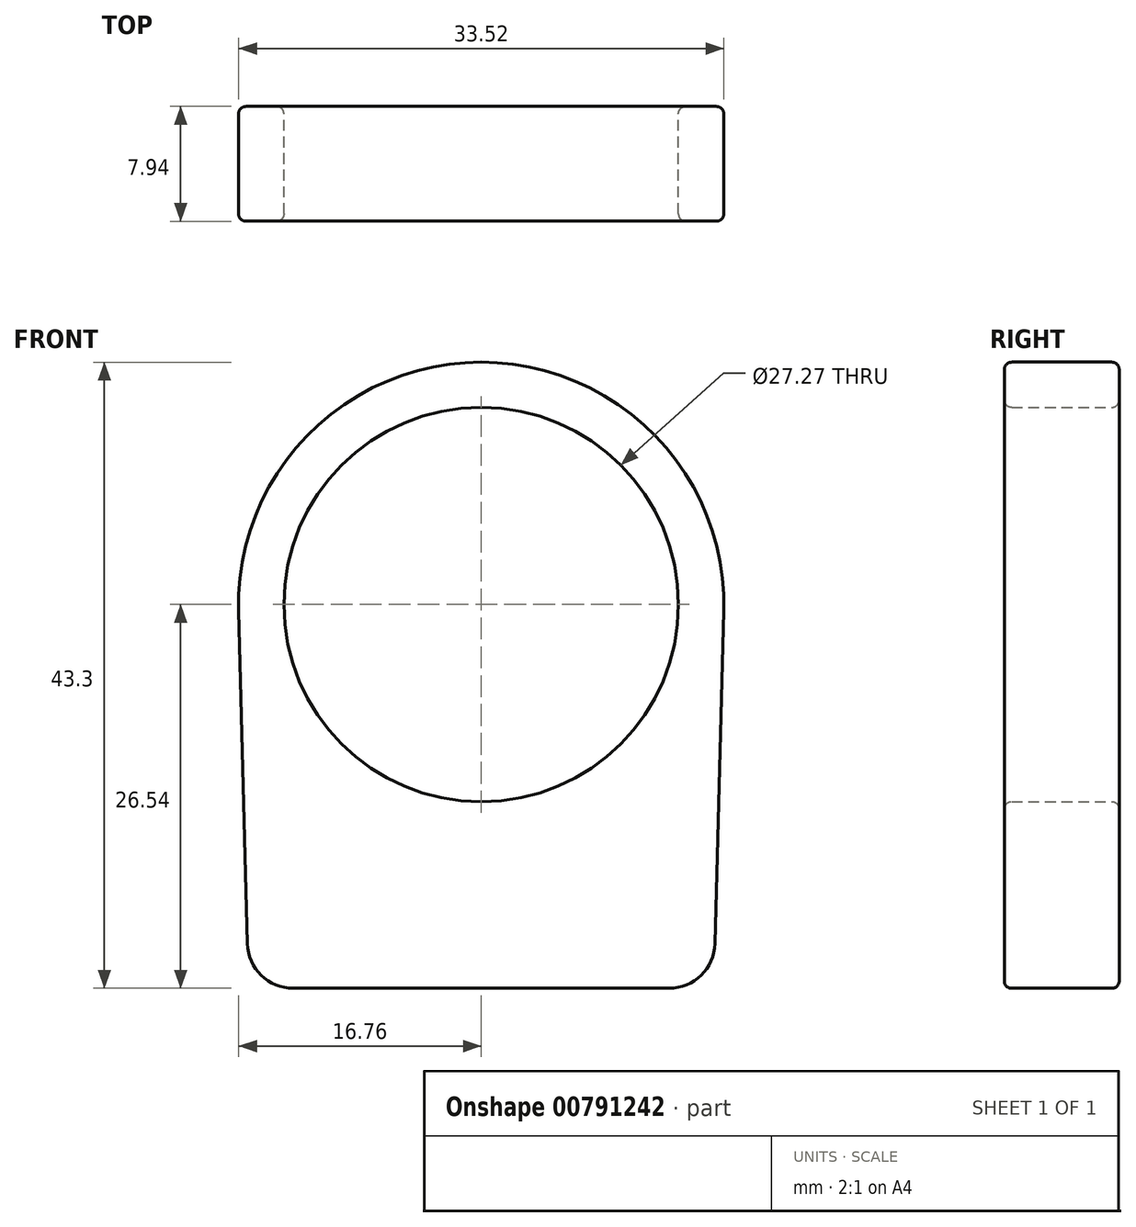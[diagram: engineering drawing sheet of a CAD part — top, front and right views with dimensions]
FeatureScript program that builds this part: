
annotation { "Feature Type Name" : "Feature", "Feature Type Description" : "" }
export const myFeature = defineFeature(function(context is Context, id is Id, definition is map)
    precondition{}
    {
        {
            var Q0;
            Q0=qCreatedBy(makeId("Front.planeOp"),FACE);
            var sketch = newSketch(context, id + "F0", { "sketchPlane" : qUnion([Q0])});
            skCircle(sketch, "E0", {"center": v(0, 0) * mm, "radius": 13.63 * mm});
            skArc(sketch, "E1", {"start": v(16.76, -0.44) * mm, "mid": v(0, 16.76) * mm, "end": v(-16.76, -0.44) * mm});
            skLineSegment(sketch, "E2", {"start": v(-12.98, -26.54) * mm, "end": v(12.98, -26.54) * mm});
            skLineSegment(sketch, "E3", {"start": v(-16.16, -23.45) * mm, "end": v(-16.76, -0.44) * mm});
            skLineSegment(sketch, "E4", {"start": v(16.16, -23.45) * mm, "end": v(16.76, -0.44) * mm});
            skPoint(sketch, "E5", {"position": v(0, -26.54) * mm});
            skPoint(sketch, "E6.visualSharp", {"position": v(-16.07, -26.54) * mm});
            skArc(sketch, "E6.filletArc", {"start": v(-16.16, -23.45) * mm, "mid": v(-15.2, -25.64) * mm, "end": v(-12.98, -26.54) * mm});
            skPoint(sketch, "E7.visualSharp", {"position": v(16.07, -26.54) * mm});
            skArc(sketch, "E7.filletArc", {"start": v(12.98, -26.54) * mm, "mid": v(15.2, -25.64) * mm, "end": v(16.16, -23.45) * mm});
            skSolve(sketch);
        }
        {
            var Q0;
            Q0=qSketchRegion(id+"F0",true);
            extrude(context, id + "F1", {"entities" : qUnion([Q0]), "endBound" : BoundingType.SYMMETRIC, "depth" : 7.94 * mm});
        }
        {
            var Q0;
            Q0=makeQuery(id+"F1.opExtrude","CAP_FACE",FACE,{"disambiguationData":[OSD([sQuery(id+"F0.wireOp",EDGE,"E0"),sQuery(id+"F0.wireOp",EDGE,"E1"),sQuery(id+"F0.wireOp",EDGE,"E2"),sQuery(id+"F0.wireOp",EDGE,"E3"),sQuery(id+"F0.wireOp",EDGE,"E4"),sQuery(id+"F0.wireOp",EDGE,"E6.filletArc"),sQuery(id+"F0.wireOp",EDGE,"E7.filletArc")])],"isStart":false});
            var Q1;
            Q1=makeQuery(id+"F1.opExtrude","CAP_FACE",FACE,{"disambiguationData":[OSD([sQuery(id+"F0.wireOp",EDGE,"E0"),sQuery(id+"F0.wireOp",EDGE,"E1"),sQuery(id+"F0.wireOp",EDGE,"E2"),sQuery(id+"F0.wireOp",EDGE,"E3"),sQuery(id+"F0.wireOp",EDGE,"E4"),sQuery(id+"F0.wireOp",EDGE,"E6.filletArc"),sQuery(id+"F0.wireOp",EDGE,"E7.filletArc")])],"isStart":true});
            fillet(context, id + "F2", {"entities" : qUnion([Q0, Q1]), "radius" : 0.5 * mm, "tangentPropagation" : true, "allowEdgeOverflow" : false});
        }
    });
